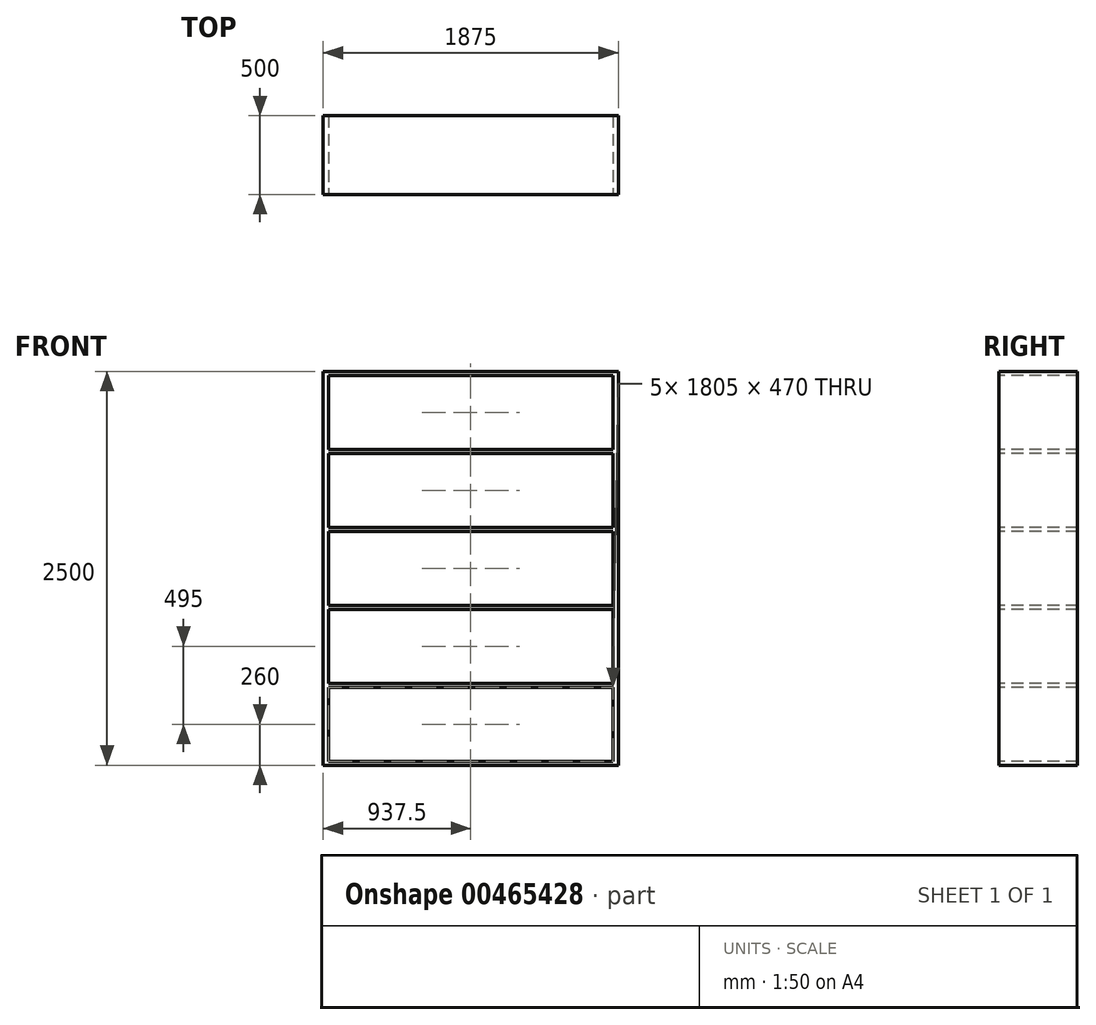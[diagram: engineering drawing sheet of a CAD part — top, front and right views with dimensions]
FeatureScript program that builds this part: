
annotation { "Feature Type Name" : "Feature", "Feature Type Description" : "" }
export const myFeature = defineFeature(function(context is Context, id is Id, definition is map)
    precondition{}
    {
        {
            var Q0;
            Q0=qCreatedBy(makeId("Top.planeOp"),FACE);
            var sketch = newSketch(context, id + "F0", { "sketchPlane" : qUnion([Q0])});
            skLineSegment(sketch, "E0.bottom", {"start": v(0, 0) * mm, "end": v(1875, 0) * mm});
            skLineSegment(sketch, "E0.top", {"start": v(0, 500) * mm, "end": v(1875, 500) * mm});
            skLineSegment(sketch, "E0.left", {"start": v(0, 0) * mm, "end": v(0, 500) * mm});
            skLineSegment(sketch, "E0.right", {"start": v(1875, 0) * mm, "end": v(1875, 500) * mm});
            skSolve(sketch);
        }
        {
            var Q0;
            Q0=makeQuery(id+"F0.imprint","IMPRINT",FACE,{"disambiguationData":[TD([[makeQuery(id+"F0.imprint","IMPRINT",EDGE,{"derivedFrom":sQuery(id+"F0.wireOp",EDGE,"E0.bottom")}),1.0]])]});
            extrude(context, id + "F1", {"entities" : qUnion([Q0]), "depth" : 2500 * mm});
        }
        {
            var Q0;
            Q0=makeQuery(id+"F1.opExtrude","SWEPT_FACE",FACE,{"disambiguationData":[OSD([sQuery(id+"F0.wireOp",EDGE,"E0.bottom")])]});
            var sketch = newSketch(context, id + "F2", { "sketchPlane" : qUnion([Q0])});
            skLineSegment(sketch, "E1.bottom", {"start": v(35, 25) * mm, "end": v(1840, 25) * mm});
            skLineSegment(sketch, "E1.top", {"start": v(35, 495) * mm, "end": v(1840, 495) * mm});
            skLineSegment(sketch, "E1.left", {"start": v(35, 25) * mm, "end": v(35, 495) * mm});
            skLineSegment(sketch, "E1.right", {"start": v(1840, 25) * mm, "end": v(1840, 495) * mm});
            skLineSegment(sketch, "E2.0.1.0", {"start": v(35, 520) * mm, "end": v(1840, 520) * mm});
            skLineSegment(sketch, "E2.0.1.1", {"start": v(35, 990) * mm, "end": v(1840, 990) * mm});
            skLineSegment(sketch, "E2.0.1.2", {"start": v(35, 520) * mm, "end": v(35, 990) * mm});
            skLineSegment(sketch, "E2.0.1.3", {"start": v(1840, 520) * mm, "end": v(1840, 990) * mm});
            skLineSegment(sketch, "E2.0.2.0", {"start": v(35, 1015) * mm, "end": v(1840, 1015) * mm});
            skLineSegment(sketch, "E2.0.2.1", {"start": v(35, 1485) * mm, "end": v(1840, 1485) * mm});
            skLineSegment(sketch, "E2.0.2.2", {"start": v(35, 1015) * mm, "end": v(35, 1485) * mm});
            skLineSegment(sketch, "E2.0.2.3", {"start": v(1840, 1015) * mm, "end": v(1840, 1485) * mm});
            skLineSegment(sketch, "E2.0.3.0", {"start": v(35, 1510) * mm, "end": v(1840, 1510) * mm});
            skLineSegment(sketch, "E2.0.3.1", {"start": v(35, 1980) * mm, "end": v(1840, 1980) * mm});
            skLineSegment(sketch, "E2.0.3.2", {"start": v(35, 1510) * mm, "end": v(35, 1980) * mm});
            skLineSegment(sketch, "E2.0.3.3", {"start": v(1840, 1510) * mm, "end": v(1840, 1980) * mm});
            skLineSegment(sketch, "E2.0.4.0", {"start": v(35, 2005) * mm, "end": v(1840, 2005) * mm});
            skLineSegment(sketch, "E2.0.4.1", {"start": v(35, 2475) * mm, "end": v(1840, 2475) * mm});
            skLineSegment(sketch, "E2.0.4.2", {"start": v(35, 2005) * mm, "end": v(35, 2475) * mm});
            skLineSegment(sketch, "E2.0.4.3", {"start": v(1840, 2005) * mm, "end": v(1840, 2475) * mm});
            skLineSegment(sketch, "E2.direction1", {"start": v(35, 25) * mm, "end": v(50, 25) * mm, "construction": true});
            skLineSegment(sketch, "E2.direction2", {"start": v(35, 25) * mm, "end": v(35, 520) * mm, "construction": true});
            skSolve(sketch);
        }
        {
            var Q0;
            Q0 = qSketchRegion(id + "F2", true);
            extrude(context, id + "F3", {"entities" : qUnion([Q0]), "operationType" : NewBodyOperationType.REMOVE, "oppositeDirection" : true, "depth" : 600 * mm});
        }
    });
